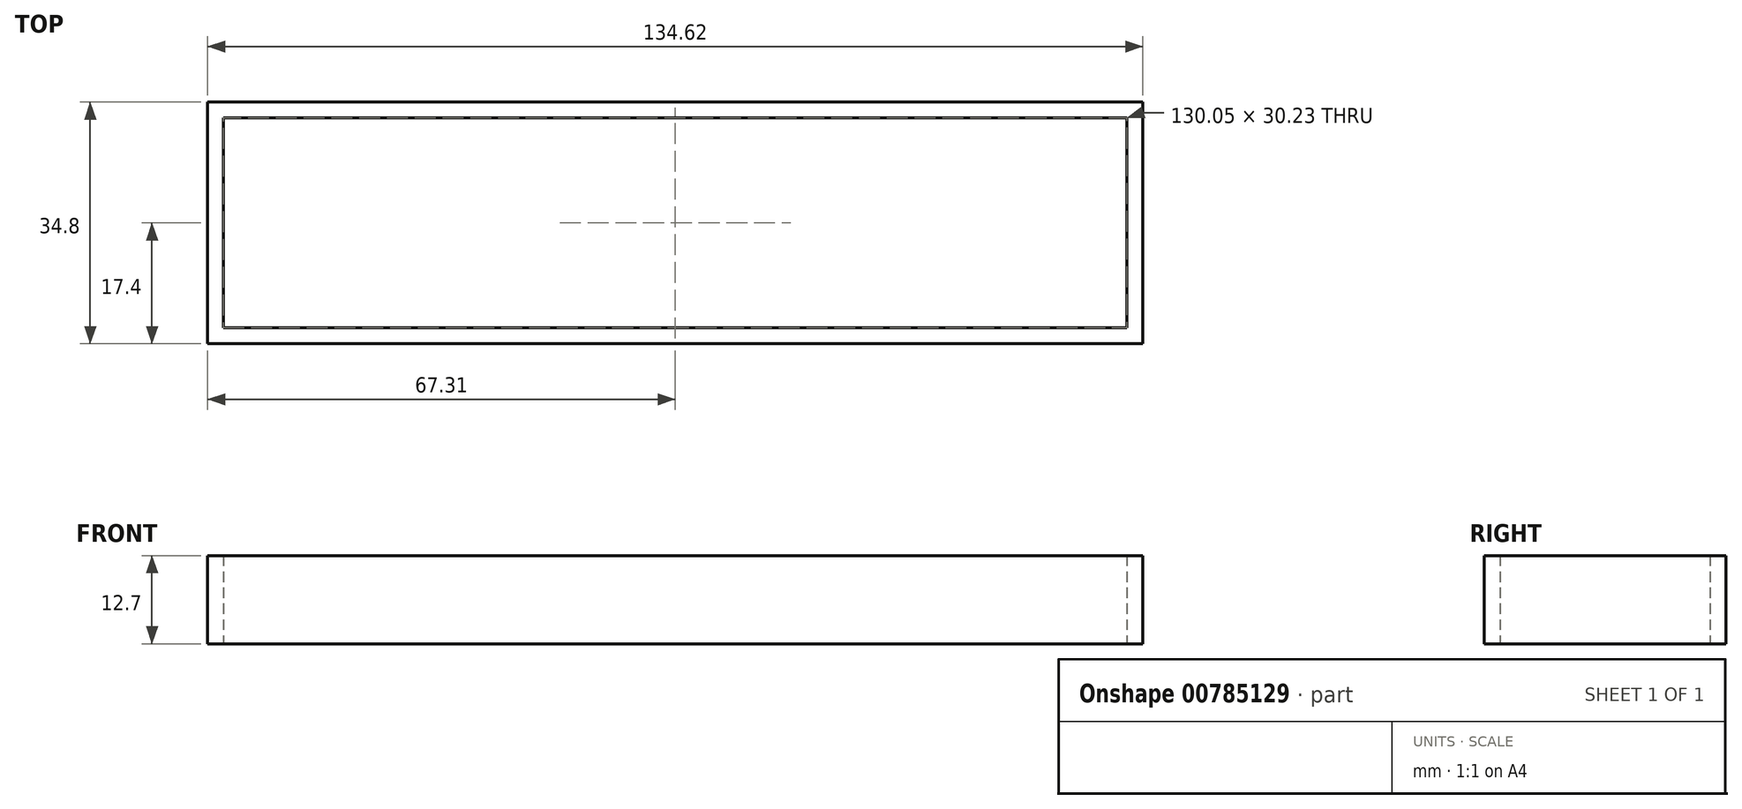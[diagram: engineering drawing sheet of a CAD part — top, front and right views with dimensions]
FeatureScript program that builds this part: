
annotation { "Feature Type Name" : "Feature", "Feature Type Description" : "" }
export const myFeature = defineFeature(function(context is Context, id is Id, definition is map)
    precondition{}
    {
        {
            var Q0;
            Q0=qCreatedBy(makeId("Top.planeOp"),FACE);
            var sketch = newSketch(context, id + "F0", { "sketchPlane" : qUnion([Q0])});
            skLineSegment(sketch, "E0.bottom", {"start": v(-65.02, 15.11) * mm, "end": v(65.02, 15.11) * mm});
            skLineSegment(sketch, "E0.top", {"start": v(-65.02, -15.11) * mm, "end": v(65.02, -15.11) * mm});
            skLineSegment(sketch, "E0.left", {"start": v(-65.02, 15.11) * mm, "end": v(-65.02, -15.11) * mm});
            skLineSegment(sketch, "E0.right", {"start": v(65.02, 15.11) * mm, "end": v(65.02, -15.11) * mm});
            skPoint(sketch, "E0.middle", {"position": v(0, 0) * mm});
            skLineSegment(sketch, "E1.bottom", {"start": v(-67.31, 17.4) * mm, "end": v(67.31, 17.4) * mm});
            skLineSegment(sketch, "E1.top", {"start": v(-67.31, -17.4) * mm, "end": v(67.31, -17.4) * mm});
            skLineSegment(sketch, "E1.left", {"start": v(-67.31, 17.4) * mm, "end": v(-67.31, -17.4) * mm});
            skLineSegment(sketch, "E1.right", {"start": v(67.31, 17.4) * mm, "end": v(67.31, -17.4) * mm});
            skSolve(sketch);
        }
        {
            var Q0;
            Q0=makeQuery(id+"F0.imprint","IMPRINT",FACE,{"disambiguationData":[TD([[makeQuery(id+"F0.imprint","IMPRINT",EDGE,{"derivedFrom":sQuery(id+"F0.wireOp",EDGE,"E0.bottom")}),1.0]])]});
            extrude(context, id + "F1", {"entities" : qUnion([Q0]), "depth" : 12.7 * mm, "offsetDistance" : 25.4 * mm});
        }
    });
